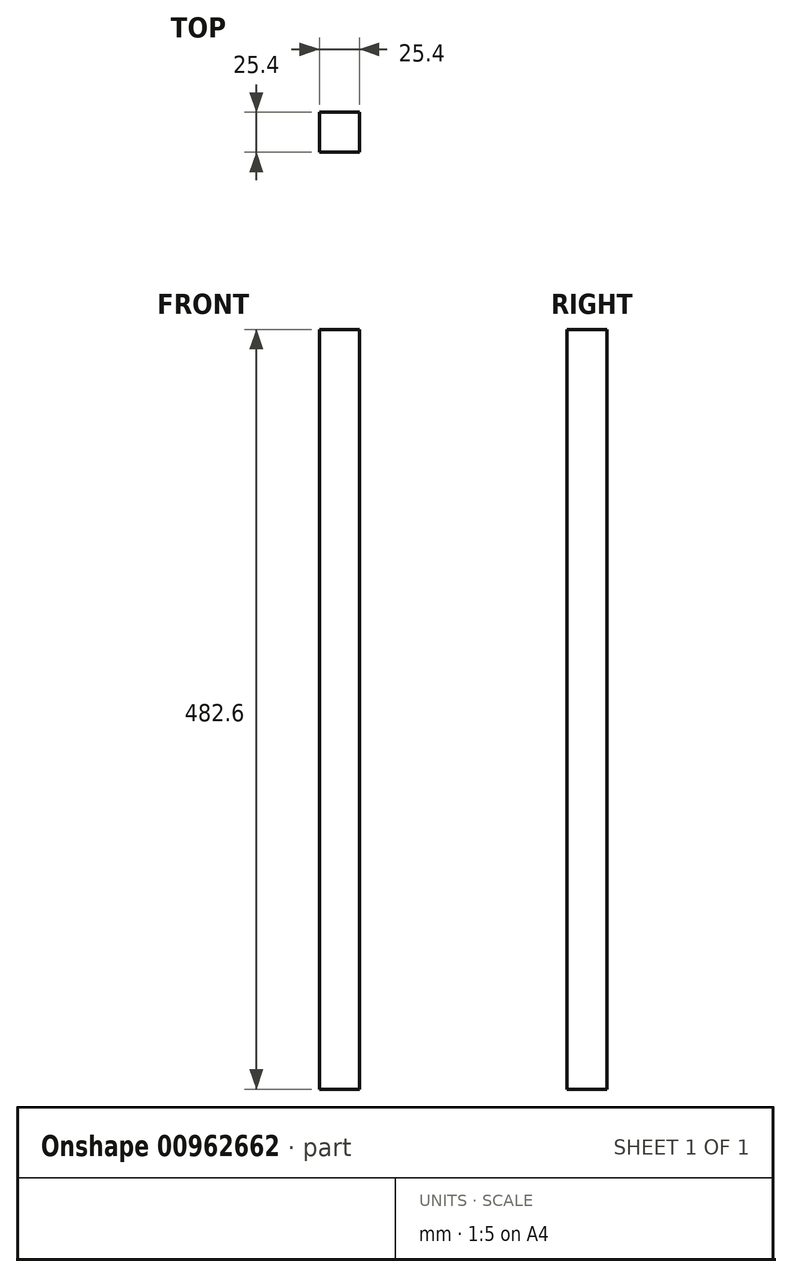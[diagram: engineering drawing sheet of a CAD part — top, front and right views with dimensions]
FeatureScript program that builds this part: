
annotation { "Feature Type Name" : "Feature", "Feature Type Description" : "" }
export const myFeature = defineFeature(function(context is Context, id is Id, definition is map)
    precondition{}
    {
        {
            var Q0;
            Q0=qCreatedBy(makeId("Front.planeOp"),FACE);
            var sketch = newSketch(context, id + "F0", { "sketchPlane" : qUnion([Q0])});
            skLineSegment(sketch, "E0.bottom", {"start": v(-12.7, 241.3) * mm, "end": v(12.7, 241.3) * mm});
            skLineSegment(sketch, "E0.top", {"start": v(-12.7, -241.3) * mm, "end": v(12.7, -241.3) * mm});
            skLineSegment(sketch, "E0.left", {"start": v(-12.7, 241.3) * mm, "end": v(-12.7, -241.3) * mm});
            skLineSegment(sketch, "E0.right", {"start": v(12.7, 241.3) * mm, "end": v(12.7, -241.3) * mm});
            skPoint(sketch, "E0.middle", {"position": v(0, 0) * mm});
            skSolve(sketch);
        }
        {
            var Q0;
            Q0=makeQuery(id+"F0.imprint","IMPRINT",FACE,{"disambiguationData":[TD([[makeQuery(id+"F0.imprint","IMPRINT",EDGE,{"derivedFrom":sQuery(id+"F0.wireOp",EDGE,"E0.bottom")}),-1.0]])]});
            extrude(context, id + "F1", {"entities" : qUnion([Q0]), "depth" : 25.4 * mm, "offsetDistance" : 25.4 * mm});
        }
    });
